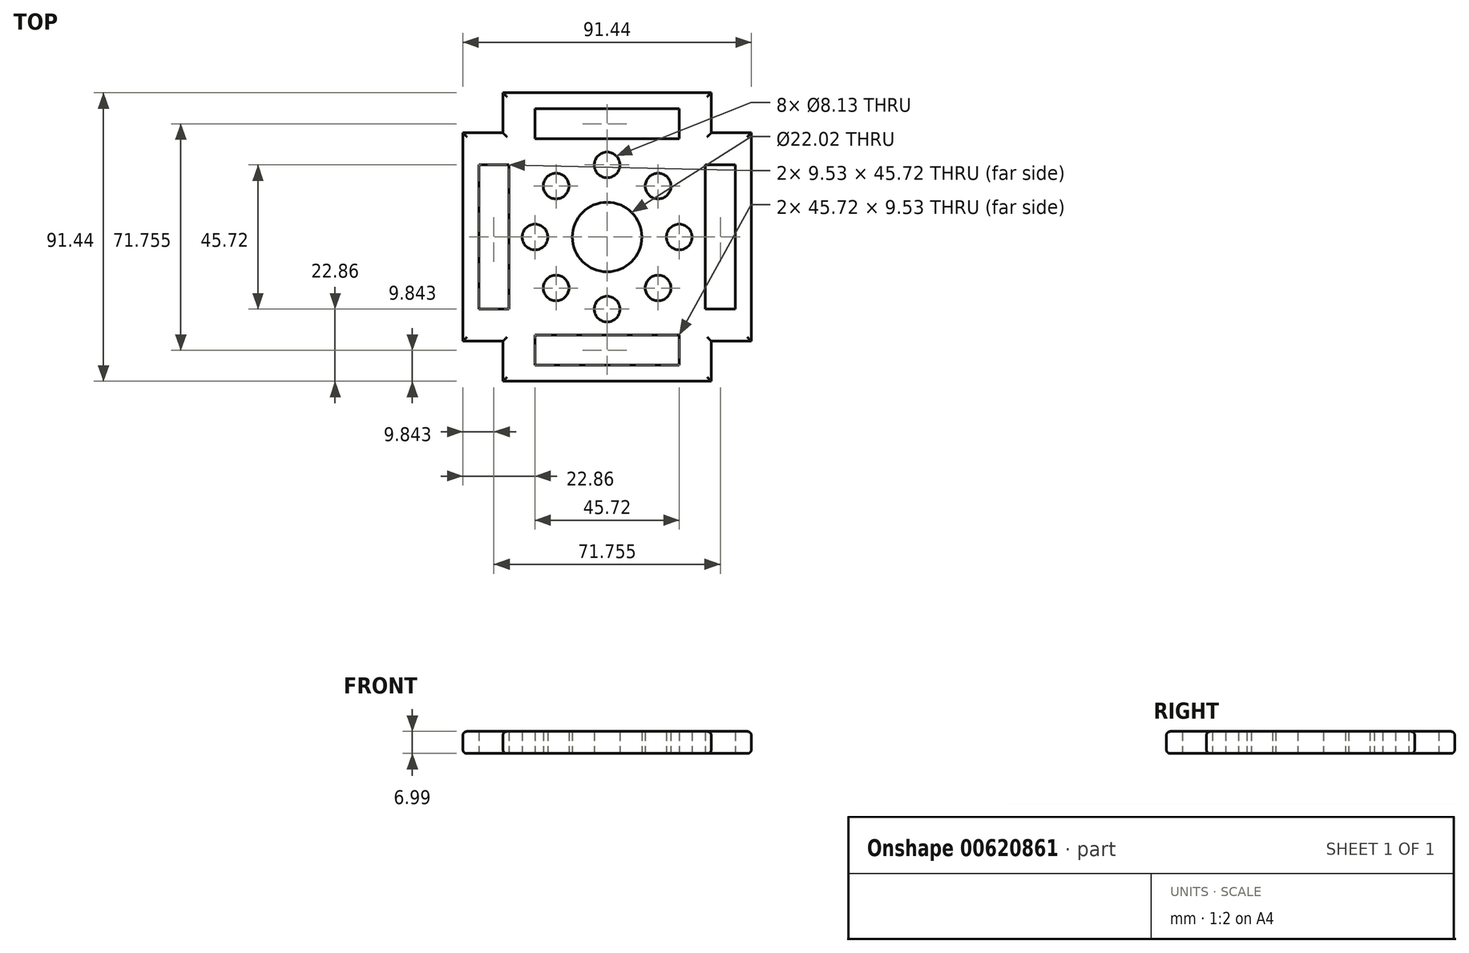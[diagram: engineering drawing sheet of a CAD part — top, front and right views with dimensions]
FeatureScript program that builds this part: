
annotation { "Feature Type Name" : "Feature", "Feature Type Description" : "" }
export const myFeature = defineFeature(function(context is Context, id is Id, definition is map)
    precondition{}
    {
        {
            var Q0;
            Q0=qCreatedBy(makeId("Top.planeOp"),FACE);
            var sketch = newSketch(context, id + "F0", { "sketchPlane" : qUnion([Q0])});
            skCircle(sketch, "E0", {"center": v(0, 0) * mm, "radius": 11.01 * mm});
            skLineSegment(sketch, "E1", {"start": v(0, 0) * mm, "end": v(0, 45.72) * mm});
            skLineSegment(sketch, "E2", {"start": v(0, 0) * mm, "end": v(45.72, 0) * mm});
            skLineSegment(sketch, "E3", {"start": v(0, 0) * mm, "end": v(-45.72, 0) * mm});
            skLineSegment(sketch, "E4", {"start": v(0, 0) * mm, "end": v(0, -45.72) * mm});
            skLineSegment(sketch, "E5", {"start": v(-33.02, 45.72) * mm, "end": v(33.02, 45.72) * mm});
            skLineSegment(sketch, "E6", {"start": v(45.72, 33.02) * mm, "end": v(45.72, -33.02) * mm});
            skLineSegment(sketch, "E7", {"start": v(33.02, -45.72) * mm, "end": v(-33.02, -45.72) * mm});
            skLineSegment(sketch, "E8", {"start": v(-45.72, 33.02) * mm, "end": v(-45.72, -33.02) * mm});
            skLineSegment(sketch, "E9", {"start": v(-45.72, 33.02) * mm, "end": v(-33.02, 33.02) * mm});
            skLineSegment(sketch, "E10", {"start": v(-33.02, 33.02) * mm, "end": v(-33.02, 45.72) * mm});
            skLineSegment(sketch, "E11", {"start": v(33.02, 45.72) * mm, "end": v(33.02, 33.02) * mm});
            skLineSegment(sketch, "E12", {"start": v(33.02, 33.02) * mm, "end": v(45.72, 33.02) * mm});
            skLineSegment(sketch, "E13", {"start": v(45.72, -33.02) * mm, "end": v(33.02, -33.02) * mm});
            skLineSegment(sketch, "E14", {"start": v(33.02, -33.02) * mm, "end": v(33.02, -45.72) * mm});
            skLineSegment(sketch, "E15", {"start": v(-33.02, -45.72) * mm, "end": v(-33.02, -33.02) * mm});
            skLineSegment(sketch, "E16", {"start": v(-33.02, -33.02) * mm, "end": v(-45.72, -33.02) * mm});
            skLineSegment(sketch, "E17.bottom", {"start": v(-40.64, 22.86) * mm, "end": v(-31.12, 22.86) * mm});
            skLineSegment(sketch, "E17.top", {"start": v(-40.64, -22.86) * mm, "end": v(-31.12, -22.86) * mm});
            skLineSegment(sketch, "E17.left", {"start": v(-40.64, 22.86) * mm, "end": v(-40.64, -22.86) * mm});
            skLineSegment(sketch, "E17.right", {"start": v(-31.12, 22.86) * mm, "end": v(-31.12, -22.86) * mm});
            skLineSegment(sketch, "E18.MirrorCS", {"start": v(40.64, 22.86) * mm, "end": v(40.64, -22.86) * mm});
            skLineSegment(sketch, "E19.MirrorCS", {"start": v(40.64, 22.86) * mm, "end": v(31.12, 22.86) * mm});
            skLineSegment(sketch, "E20.MirrorCS", {"start": v(40.64, -22.86) * mm, "end": v(31.12, -22.86) * mm});
            skLineSegment(sketch, "E21.MirrorCS", {"start": v(31.12, 22.86) * mm, "end": v(31.12, -22.86) * mm});
            skLineSegment(sketch, "E22.bottom", {"start": v(-22.86, -40.64) * mm, "end": v(-22.86, -31.12) * mm});
            skLineSegment(sketch, "E22.top", {"start": v(22.86, -40.64) * mm, "end": v(22.86, -31.11) * mm});
            skLineSegment(sketch, "E22.left", {"start": v(-22.86, -40.64) * mm, "end": v(22.86, -40.64) * mm});
            skLineSegment(sketch, "E22.right", {"start": v(-22.86, -31.12) * mm, "end": v(22.86, -31.12) * mm});
            skLineSegment(sketch, "E23.MirrorCS", {"start": v(-22.86, 40.64) * mm, "end": v(22.86, 40.64) * mm});
            skLineSegment(sketch, "E24.MirrorCS", {"start": v(-22.86, 31.12) * mm, "end": v(22.86, 31.12) * mm});
            skLineSegment(sketch, "E25.MirrorCS", {"start": v(-22.86, 40.64) * mm, "end": v(-22.86, 31.12) * mm});
            skLineSegment(sketch, "E26.MirrorCS", {"start": v(22.86, 40.64) * mm, "end": v(22.86, 31.11) * mm});
            skCircle(sketch, "E27", {"center": v(0, 22.86) * mm, "radius": 4.06 * mm});
            skCircle(sketch, "E28.1.0", {"center": v(-16.16, 16.16) * mm, "radius": 4.06 * mm});
            skCircle(sketch, "E28.2.0", {"center": v(-22.86, 0) * mm, "radius": 4.06 * mm});
            skCircle(sketch, "E28.3.0", {"center": v(-16.16, -16.16) * mm, "radius": 4.06 * mm});
            skCircle(sketch, "E28.4.0", {"center": v(0, -22.86) * mm, "radius": 4.06 * mm});
            skCircle(sketch, "E28.5.0", {"center": v(16.16, -16.16) * mm, "radius": 4.06 * mm});
            skCircle(sketch, "E28.6.0", {"center": v(22.86, 0) * mm, "radius": 4.06 * mm});
            skCircle(sketch, "E28.7.0", {"center": v(16.16, 16.16) * mm, "radius": 4.06 * mm});
            skSolve(sketch);
        }
        {
            var Q0;
            {var subQ0=sQuery(id+"F0.wireOp",EDGE,"E9");Q0=makeQuery(id+"F0.imprint","IMPRINT",FACE,{"disambiguationData":[TD([[makeQuery(id+"F0.imprint","IMPRINT",EDGE,{"derivedFrom":subQ0}),-1.0]])]});}
            var Q1;
            {var subQ11=sQuery(id+"F0.wireOp",EDGE,"E11");Q1=makeQuery(id+"F0.imprint","IMPRINT",FACE,{"disambiguationData":[TD([[makeQuery(id+"F0.imprint","IMPRINT",EDGE,{"derivedFrom":subQ11}),-1.0]])]});}
            var Q2;
            {var subQ0=sQuery(id+"F0.wireOp",EDGE,"E13");Q2=makeQuery(id+"F0.imprint","IMPRINT",FACE,{"disambiguationData":[TD([[makeQuery(id+"F0.imprint","IMPRINT",EDGE,{"derivedFrom":subQ0}),-1.0]])]});}
            var Q3;
            {var subQ0=sQuery(id+"F0.wireOp",EDGE,"E15");Q3=makeQuery(id+"F0.imprint","IMPRINT",FACE,{"disambiguationData":[TD([[makeQuery(id+"F0.imprint","IMPRINT",EDGE,{"derivedFrom":subQ0}),-1.0]])]});}
            extrude(context, id + "F1", {"entities" : qUnion([Q0, Q1, Q2, Q3]), "depth" : 7 * mm, "offsetDistance" : 25.4 * mm});
        }
        {
            var Q0;
            Q0=makeQuery(id+"F1.opExtrude","CAP_EDGE",EDGE,{"disambiguationData":[OSD([sQuery(id+"F0.wireOp",EDGE,"E5")])],"isStart":false});
            var Q1;
            Q1=makeQuery(id+"F1.opExtrude","CAP_EDGE",EDGE,{"disambiguationData":[OSD([sQuery(id+"F0.wireOp",EDGE,"E10")])],"isStart":false});
            var Q2;
            Q2=makeQuery(id+"F1.opExtrude","CAP_EDGE",EDGE,{"disambiguationData":[OSD([sQuery(id+"F0.wireOp",EDGE,"E9")])],"isStart":false});
            var Q3;
            Q3=makeQuery(id+"F1.opExtrude","CAP_EDGE",EDGE,{"disambiguationData":[OSD([sQuery(id+"F0.wireOp",EDGE,"E8")])],"isStart":false});
            var Q4;
            Q4=makeQuery(id+"F1.opExtrude","CAP_EDGE",EDGE,{"disambiguationData":[OSD([sQuery(id+"F0.wireOp",EDGE,"E15")])],"isStart":false});
            var Q5;
            Q5=makeQuery(id+"F1.opExtrude","CAP_EDGE",EDGE,{"disambiguationData":[OSD([sQuery(id+"F0.wireOp",EDGE,"E16")])],"isStart":false});
            var Q6;
            Q6=makeQuery(id+"F1.opExtrude","CAP_EDGE",EDGE,{"disambiguationData":[OSD([sQuery(id+"F0.wireOp",EDGE,"E7")])],"isStart":false});
            var Q7;
            Q7=makeQuery(id+"F1.opExtrude","CAP_EDGE",EDGE,{"disambiguationData":[OSD([sQuery(id+"F0.wireOp",EDGE,"E14")])],"isStart":false});
            var Q8;
            Q8=makeQuery(id+"F1.opExtrude","CAP_EDGE",EDGE,{"disambiguationData":[OSD([sQuery(id+"F0.wireOp",EDGE,"E13")])],"isStart":false});
            var Q9;
            Q9=makeQuery(id+"F1.opExtrude","CAP_EDGE",EDGE,{"disambiguationData":[OSD([sQuery(id+"F0.wireOp",EDGE,"E6")])],"isStart":false});
            var Q10;
            Q10=makeQuery(id+"F1.opExtrude","CAP_EDGE",EDGE,{"disambiguationData":[OSD([sQuery(id+"F0.wireOp",EDGE,"E12")])],"isStart":false});
            var Q11;
            Q11=makeQuery(id+"F1.opExtrude","CAP_EDGE",EDGE,{"disambiguationData":[OSD([sQuery(id+"F0.wireOp",EDGE,"E11")])],"isStart":false});
            var Q12;
            Q12=makeQuery(id+"F1.opExtrude","CAP_EDGE",EDGE,{"disambiguationData":[OSD([sQuery(id+"F0.wireOp",EDGE,"E7")])],"isStart":true});
            var Q13;
            Q13=makeQuery(id+"F1.opExtrude","CAP_EDGE",EDGE,{"disambiguationData":[OSD([sQuery(id+"F0.wireOp",EDGE,"E15")])],"isStart":true});
            var Q14;
            Q14=makeQuery(id+"F1.opExtrude","CAP_EDGE",EDGE,{"disambiguationData":[OSD([sQuery(id+"F0.wireOp",EDGE,"E16")])],"isStart":true});
            var Q15;
            Q15=makeQuery(id+"F1.opExtrude","CAP_EDGE",EDGE,{"disambiguationData":[OSD([sQuery(id+"F0.wireOp",EDGE,"E8")])],"isStart":true});
            var Q16;
            Q16=makeQuery(id+"F1.opExtrude","CAP_EDGE",EDGE,{"disambiguationData":[OSD([sQuery(id+"F0.wireOp",EDGE,"E9")])],"isStart":true});
            var Q17;
            Q17=makeQuery(id+"F1.opExtrude","CAP_EDGE",EDGE,{"disambiguationData":[OSD([sQuery(id+"F0.wireOp",EDGE,"E10")])],"isStart":true});
            var Q18;
            Q18=makeQuery(id+"F1.opExtrude","CAP_EDGE",EDGE,{"disambiguationData":[OSD([sQuery(id+"F0.wireOp",EDGE,"E5")])],"isStart":true});
            var Q19;
            Q19=makeQuery(id+"F1.opExtrude","CAP_EDGE",EDGE,{"disambiguationData":[OSD([sQuery(id+"F0.wireOp",EDGE,"E11")])],"isStart":true});
            var Q20;
            Q20=makeQuery(id+"F1.opExtrude","CAP_EDGE",EDGE,{"disambiguationData":[OSD([sQuery(id+"F0.wireOp",EDGE,"E12")])],"isStart":true});
            var Q21;
            Q21=makeQuery(id+"F1.opExtrude","CAP_EDGE",EDGE,{"disambiguationData":[OSD([sQuery(id+"F0.wireOp",EDGE,"E6")])],"isStart":true});
            var Q22;
            Q22=makeQuery(id+"F1.opExtrude","CAP_EDGE",EDGE,{"disambiguationData":[OSD([sQuery(id+"F0.wireOp",EDGE,"E13")])],"isStart":true});
            var Q23;
            Q23=makeQuery(id+"F1.opExtrude","CAP_EDGE",EDGE,{"disambiguationData":[OSD([sQuery(id+"F0.wireOp",EDGE,"E14")])],"isStart":true});
            fillet(context, id + "F2", {"entities" : qUnion([Q0, Q1, Q2, Q3, Q4, Q5, Q6, Q7, Q8, Q9, Q10, Q11, Q12, Q13, Q14, Q15, Q16, Q17, Q18, Q19, Q20, Q21, Q22, Q23]), "radius" : 1.27 * mm, "tangentPropagation" : true, "allowEdgeOverflow" : false});
        }
    });
